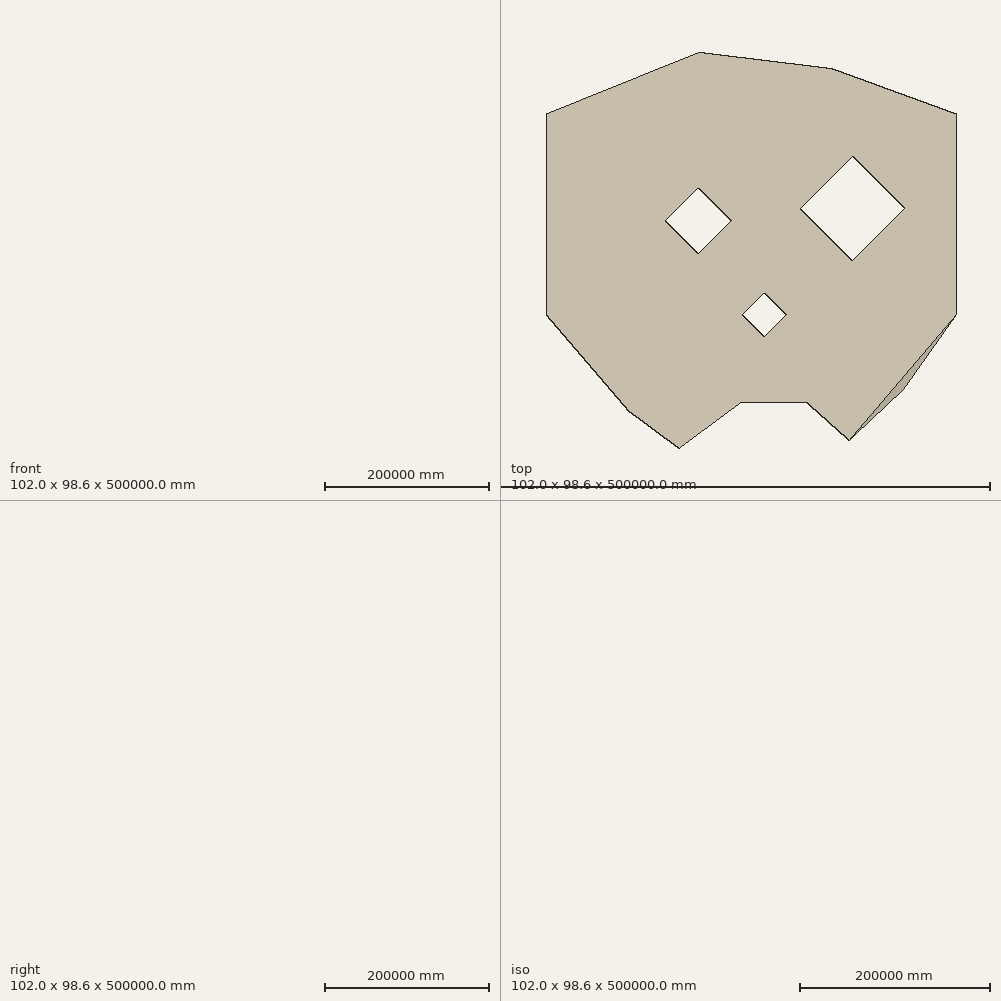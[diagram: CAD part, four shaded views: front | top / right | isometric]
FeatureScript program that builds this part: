
annotation { "Feature Type Name" : "Feature", "Feature Type Description" : "" }
export const myFeature = defineFeature(function(context is Context, id is Id, definition is map)
    precondition{}
    {
        {
            var Q0;
            Q0=qCreatedBy(makeId("Top.planeOp"),FACE);
            var sketch = newSketch(context, id + "F0", { "sketchPlane" : qUnion([Q0])});
            skFitSpline(sketch, "E0", {"points": [v(-54.3, 0) * mm, v(47.7, 0) * mm], "startDerivative": vector(109.43, -155.23) * mm, "endDerivative": vector(94.5, 156.88) * mm});
            skLineSegment(sketch, "E1", {"start": v(-54.3, 0) * mm, "end": v(-54.3, 50) * mm});
            skLineSegment(sketch, "E2", {"start": v(47.7, 0) * mm, "end": v(47.7, 50) * mm});
            skCircle(sketch, "E3", {"center": v(-16.49, 23.36) * mm, "radius": 8.23 * mm});
            skCircle(sketch, "E4", {"center": v(21.94, 26.45) * mm, "radius": 12.99 * mm});
            skLineSegment(sketch, "E5", {"start": v(-54.3, 50) * mm, "end": v(-16.25, 65.35) * mm});
            skLineSegment(sketch, "E6", {"start": v(47.7, 50) * mm, "end": v(16.72, 61.32) * mm});
            skLineSegment(sketch, "E7", {"start": v(16.72, 61.32) * mm, "end": v(-16.25, 65.35) * mm});
            skCircle(sketch, "E8", {"center": v(0, 0) * mm, "radius": 5.44 * mm});
            skLineSegment(sketch, "E9", {"start": v(-33.8, -23.92) * mm, "end": v(-23.13, -34.58) * mm});
            skLineSegment(sketch, "E10", {"start": v(28.82, -38.16) * mm, "end": v(10.4, -21.71) * mm});
            skLineSegment(sketch, "E11", {"start": v(10.4, -21.71) * mm, "end": v(-5.8, -21.75) * mm});
            skLineSegment(sketch, "E12", {"start": v(-5.8, -21.75) * mm, "end": v(-23.13, -34.58) * mm});
            skLineSegment(sketch, "E13", {"start": v(47.7, 0) * mm, "end": v(28.82, -38.16) * mm});
            skSolve(sketch);
        }
        {
            var Q0;
            Q0=makeQuery(id+"F0.imprint","IMPRINT",FACE,{"disambiguationData":[TD([[makeQuery(id+"F0.imprint","IMPRINT",EDGE,{"derivedFrom":sQuery(id+"F0.wireOp",EDGE,"E0")}),1.0]])]});
            extrude(context, id + "F1", {"entities" : qUnion([Q0]), "depth" : 500000 * mm, "offsetDistance" : 25 * mm});
        }
    });
